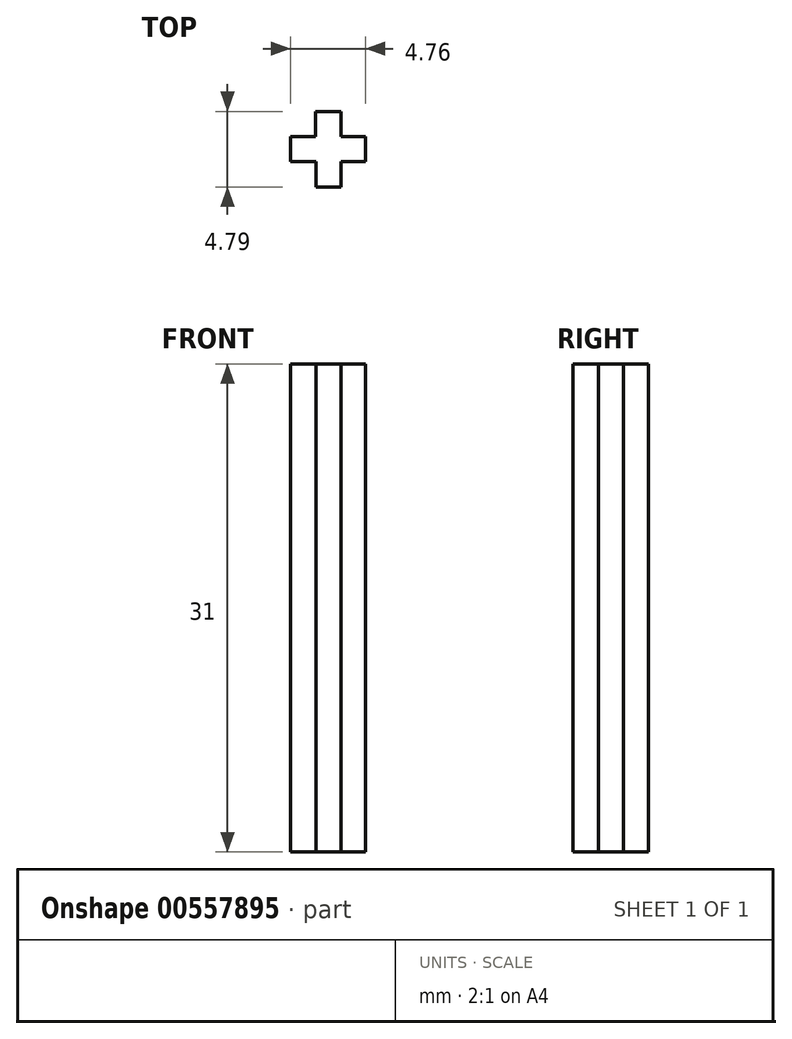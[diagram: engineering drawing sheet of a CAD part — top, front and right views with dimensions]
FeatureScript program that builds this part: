
annotation { "Feature Type Name" : "Feature", "Feature Type Description" : "" }
export const myFeature = defineFeature(function(context is Context, id is Id, definition is map)
    precondition{}
    {
        {
            var Q0;
            Q0=qCreatedBy(makeId("Top.planeOp"),FACE);
            var sketch = newSketch(context, id + "F0", { "sketchPlane" : qUnion([Q0])});
            skLineSegment(sketch, "E0", {"start": v(-2.81, -1.84) * mm, "end": v(1.95, -1.84) * mm});
            skLineSegment(sketch, "E1", {"start": v(-2.81, -3.42) * mm, "end": v(1.95, -3.42) * mm});
            skLineSegment(sketch, "E2", {"start": v(-2.81, -1.84) * mm, "end": v(-2.81, -3.42) * mm});
            skLineSegment(sketch, "E3", {"start": v(1.95, -1.84) * mm, "end": v(1.95, -3.42) * mm});
            skLineSegment(sketch, "E4", {"start": v(-1.21, -1.84) * mm, "end": v(-2.81, -1.84) * mm});
            skLineSegment(sketch, "E5", {"start": v(1.95, -1.84) * mm, "end": v(0.35, -1.84) * mm});
            skLineSegment(sketch, "E6", {"start": v(-1.21, -1.84) * mm, "end": v(-1.21, -0.23) * mm});
            skLineSegment(sketch, "E7", {"start": v(-1.21, -0.23) * mm, "end": v(0.4, -0.23) * mm});
            skLineSegment(sketch, "E8", {"start": v(0.4, -0.23) * mm, "end": v(0.4, -1.84) * mm});
            skLineSegment(sketch, "E9", {"start": v(0.4, -1.84) * mm, "end": v(0.4, -3.42) * mm});
            skLineSegment(sketch, "E10", {"start": v(0.4, -3.42) * mm, "end": v(0.4, -5.02) * mm});
            skLineSegment(sketch, "E11", {"start": v(0.4, -5.02) * mm, "end": v(-1.2, -5.02) * mm});
            skLineSegment(sketch, "E12", {"start": v(-1.2, -5.02) * mm, "end": v(-1.2, -3.42) * mm});
            skSolve(sketch);
        }
        {
            var Q0;
            Q0 = qSketchRegion(id + "F0", true);
            extrude(context, id + "F1", {"entities" : qUnion([Q0]), "depth" : 31 * mm, "offsetDistance" : 25.4 * mm});
        }
    });
